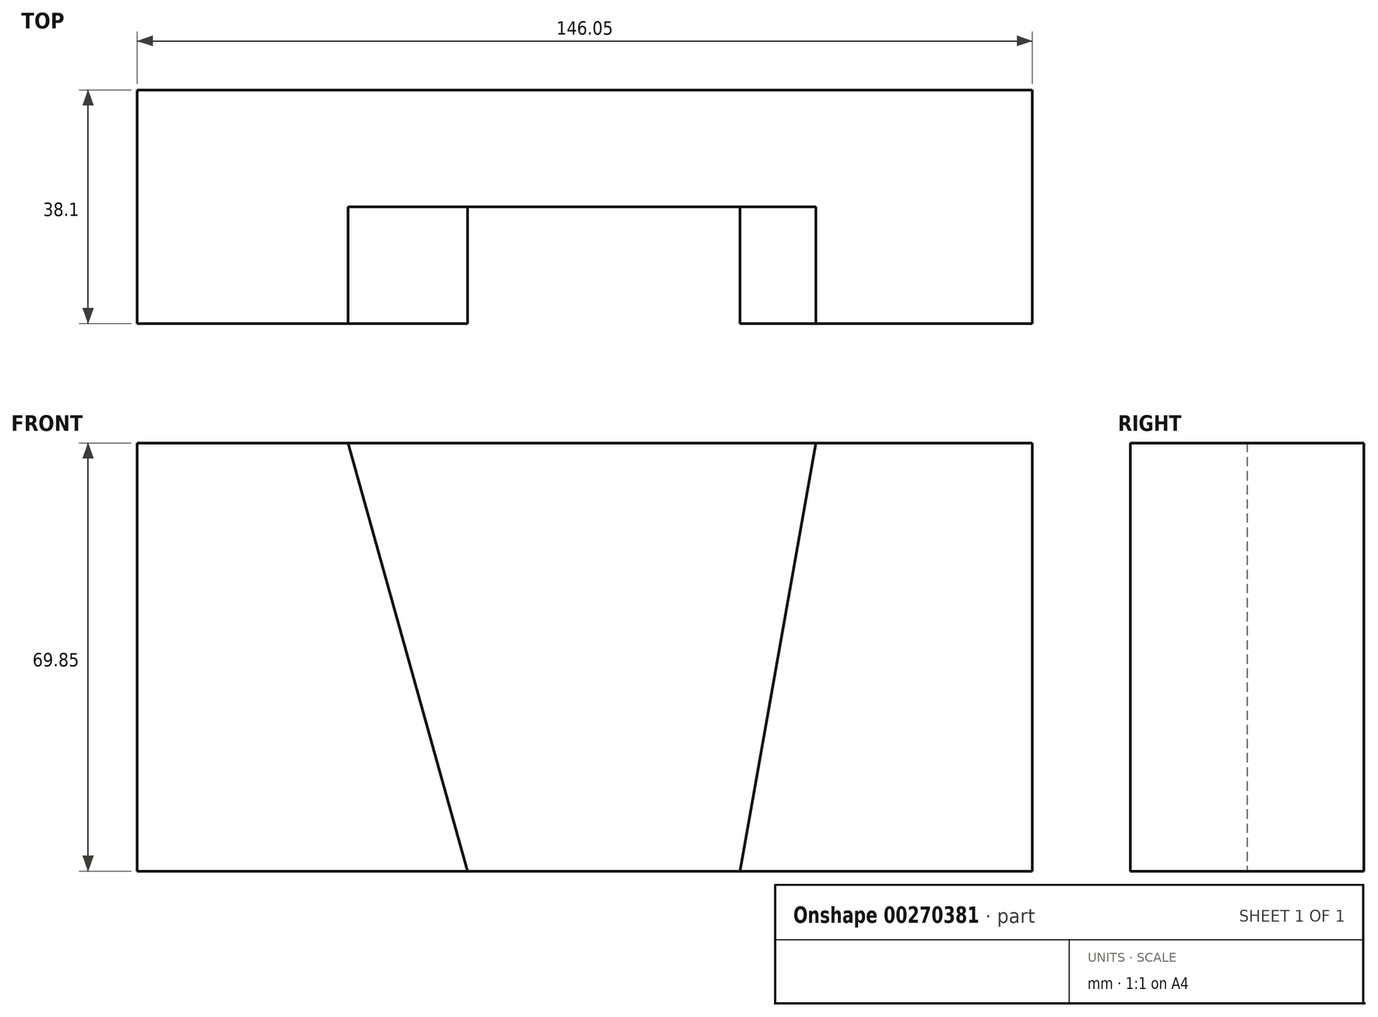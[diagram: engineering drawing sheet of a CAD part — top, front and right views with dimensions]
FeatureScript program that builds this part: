
annotation { "Feature Type Name" : "Feature", "Feature Type Description" : "" }
export const myFeature = defineFeature(function(context is Context, id is Id, definition is map)
    precondition{}
    {
        {
            var Q0;
            Q0=qCreatedBy(makeId("Front.planeOp"),FACE);
            var sketch = newSketch(context, id + "F0", { "sketchPlane" : qUnion([Q0])});
            skLineSegment(sketch, "E0", {"start": v(-77.4, -69.85) * mm, "end": v(68.65, -69.85) * mm});
            skLineSegment(sketch, "E1", {"start": v(-77.4, -69.85) * mm, "end": v(-77.4, 0) * mm});
            skLineSegment(sketch, "E2", {"start": v(-77.4, 0) * mm, "end": v(68.65, 0) * mm});
            skLineSegment(sketch, "E3", {"start": v(68.65, 0) * mm, "end": v(68.65, -69.85) * mm});
            skSolve(sketch);
        }
        {
            var Q0;
            Q0 = qSketchRegion(id + "F0", true);
            extrude(context, id + "F1", {"entities" : qUnion([Q0]), "depth" : 38.1 * mm});
        }
        {
            var Q0;
            Q0=makeQuery(id+"F1.opExtrude","CAP_FACE",FACE,{"disambiguationData":[OSD([sQuery(id+"F0.wireOp",EDGE,"E0"),sQuery(id+"F0.wireOp",EDGE,"E1"),sQuery(id+"F0.wireOp",EDGE,"E2"),sQuery(id+"F0.wireOp",EDGE,"E3")])],"isStart":false});
            var sketch = newSketch(context, id + "F2", { "sketchPlane" : qUnion([Q0])});
            skLineSegment(sketch, "E4", {"start": v(-23.49, -69.85) * mm, "end": v(20.96, -69.85) * mm});
            skLineSegment(sketch, "E5", {"start": v(-43.01, 0) * mm, "end": v(-23.49, -69.85) * mm});
            skLineSegment(sketch, "E6", {"start": v(33.35, 0) * mm, "end": v(20.96, -69.85) * mm});
            skSolve(sketch);
        }
        {
            var Q0;
            Q0 = qSketchRegion(id + "F2", true);
            var Q1;
            Q1=makeQuery(id+"F2.imprint","IMPRINT",FACE,{"disambiguationData":[TD([[makeQuery(id+"F2.imprint","IMPRINT",EDGE,{"derivedFrom":sQuery(id+"F2.wireOp",EDGE,"E4")}),1.0]])]});
            extrude(context, id + "F3", {"entities" : qUnion([Q0, Q1]), "operationType" : NewBodyOperationType.REMOVE, "oppositeDirection" : true, "depth" : 19.05 * mm});
        }
    });
